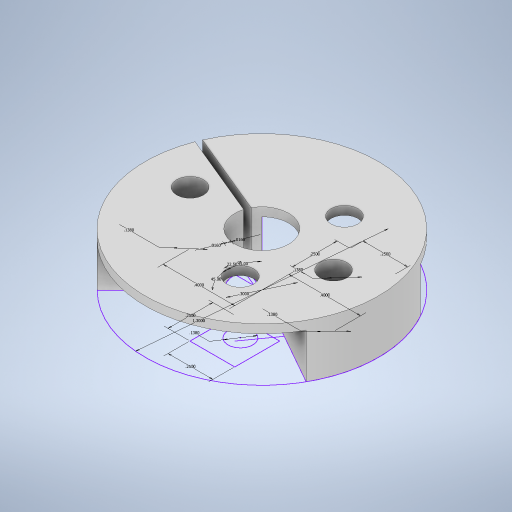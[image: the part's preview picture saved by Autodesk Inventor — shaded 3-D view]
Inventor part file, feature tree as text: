
AUTODESK INVENTOR PART (.ipt)
format: ipt  version: 2024 (Build 280153000, 153)  size: 281,088 bytes
history: native  units: in
note: dims shown in document units (in); Inventor stores cm internally (conversion verified against a paired STEP export)
features: extrude x3, sketch x1, hole x1
ambient origin geometry x8: Origin, YZ Plane, XZ Plane, XY Plane, X Axis, Y Axis, Z Axis, Center Point
bodies: Solid1 (feature_tree)
feature tree (5):
  sketch  "Sketch1"  dims[d0=0.3in d1=1.3in d2=0.25in d3=0.25in d4=0.25in d5=0.25in d6=0.138in d7=0.138in d8=0.4in d9=0.4in d10=0.138in d11=0.138in d12=45.0deg d13=45.0deg d14=0.296in d15=0.0in d16=0.248in d17=0.0in d18=0.15in d19=0.75in d20=0.279in d21=0.25in d22=0.5635in d23=1.0in d24=0.8108in d25=22.5deg d26=0.016in d27=0.016in d28=0.296in d29=0.0in]
  extrude  "Extrusion1"  Depth=0.296in
  extrude  "Extrusion2"  Depth=0.296in
  hole  "Hole1"  [1 undecoded]
  extrude  "Extrusion3"  Depth=0.296in
note: 1 required parameter value undecoded (feature->parameter linkage not recoverable at this tier; creation-order binding heuristic only, values carry confidence <= 0.55)
